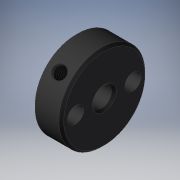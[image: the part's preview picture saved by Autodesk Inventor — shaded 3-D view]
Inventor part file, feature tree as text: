
AUTODESK INVENTOR PART (.ipt)
format: ipt  version: 2019 (Build 230136000, 136)  size: 160,768 bytes
history: native  units: mm
features: other x7, sketch x4, revolve x2, extrude x2, thread x1
ambient origin geometry x8: Origin, YZ Plane, XZ Plane, XY Plane, X Axis, Y Axis, Z Axis, Center Point
bodies: Solid1 (feature_tree)
feature tree (16):
  revolve  "Revolution1"  Angle=360.0deg
  revolve  "Revolution2"  [1 undecoded]
  thread  "Thread1"  [1 undecoded]
  extrude  "Extrusion1"  [1 undecoded]
  extrude  "Extrusion2"  [1 undecoded]
  other  "part_XY"
  other  "part_YZ"
  other  "part_ZX"
  other  "part_X"
  other  "part_Y"
  other  "part_Z"
  other  "part_Center"
  sketch  "Sketch_1"  dims[d0=360.0deg d1=360.0deg]
  sketch  "Sketch_4"  dims[d8=0.0mm]
  sketch  "Sketch_2"  dims[d2=6.7295mm d3=0.0mm d4=6.0mm d5=0.0mm d6=6.0mm d7=0.0mm]
  sketch  "Sketch_6"
note: 4 required parameter values undecoded (feature->parameter linkage not recoverable at this tier; creation-order binding heuristic only, values carry confidence <= 0.55)